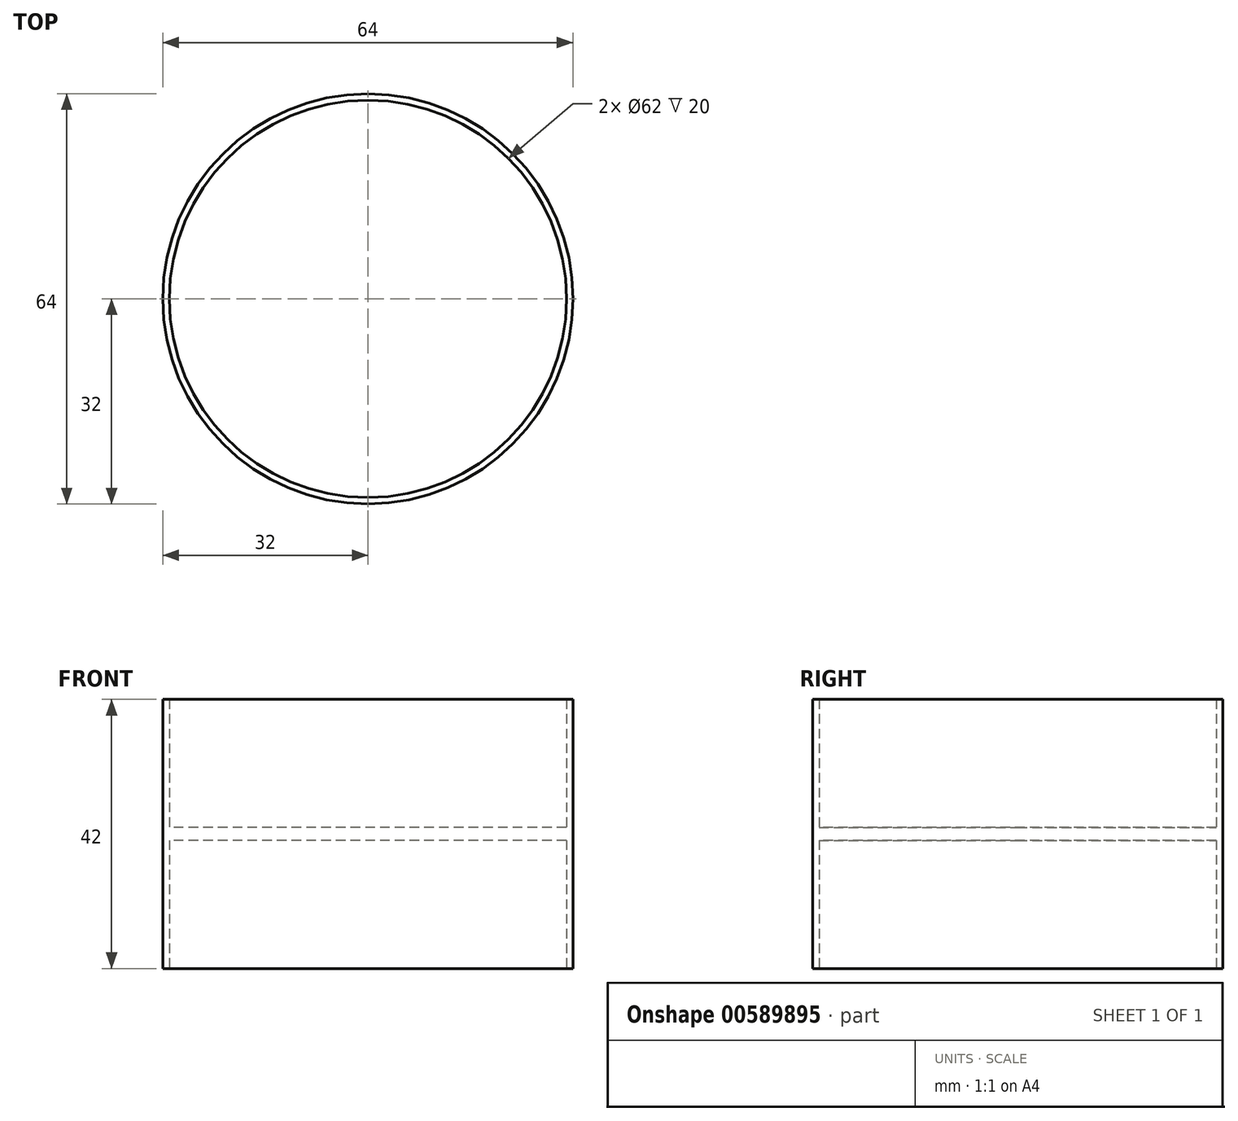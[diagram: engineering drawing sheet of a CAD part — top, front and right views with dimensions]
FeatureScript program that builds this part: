
annotation { "Feature Type Name" : "Feature", "Feature Type Description" : "" }
export const myFeature = defineFeature(function(context is Context, id is Id, definition is map)
    precondition{}
    {
        {
            var Q0;
            Q0=qCreatedBy(makeId("Top.planeOp"),FACE);
            var sketch = newSketch(context, id + "F0", { "sketchPlane" : qUnion([Q0])});
            skCircle(sketch, "E0", {"center": v(0, 0) * mm, "radius": 32 * mm});
            skCircle(sketch, "E1", {"center": v(0, 0) * mm, "radius": 34 * mm});
            skCircle(sketch, "E2", {"center": v(0, 0) * mm, "radius": 31 * mm});
            skLineSegment(sketch, "E3", {"start": v(0, 32) * mm, "end": v(0, -32) * mm});
            skSolve(sketch);
        }
        {
            var Q0;
            {var subQ0=sQuery(id+"F0.wireOp",EDGE,"E3");var subQ1=sQuery(id+"F0.wireOp",EDGE,"E0");var subQ2=makeQuery(id+"F0.imprint","INTERSECT",VERTEX,{"disambiguationData":[OD(0.0)],"derivedFrom":[subQ1,subQ0]});Q0=makeQuery(id+"F0.imprint","IMPRINT",FACE,{"disambiguationData":[TD([[makeQuery(id+"F0.imprint","IMPRINT",EDGE,{"disambiguationData":[TD([[subQ2,-1.0]])],"derivedFrom":subQ1}),1.0]])]});}
            var Q1;
            {var subQ0=sQuery(id+"F0.wireOp",EDGE,"E3");var subQ1=sQuery(id+"F0.wireOp",EDGE,"E0");var subQ2=makeQuery(id+"F0.imprint","INTERSECT",VERTEX,{"disambiguationData":[OD(0.0)],"derivedFrom":[subQ1,subQ0]});Q1=makeQuery(id+"F0.imprint","IMPRINT",FACE,{"disambiguationData":[TD([[makeQuery(id+"F0.imprint","IMPRINT",EDGE,{"disambiguationData":[TD([[subQ2,1.0]])],"derivedFrom":subQ1}),1.0]])]});}
            extrude(context, id + "F1", {"entities" : qUnion([Q0, Q1]), "depth" : 20 * mm, "offsetDistance" : 25 * mm});
        }
        {
            var Q0;
            {var subQ0=sQuery(id+"F0.wireOp",EDGE,"E3");var subQ1=sQuery(id+"F0.wireOp",EDGE,"E0");var subQ2=makeQuery(id+"F0.imprint","INTERSECT",VERTEX,{"disambiguationData":[OD(0.0)],"derivedFrom":[subQ1,subQ0]});Q0=makeQuery(id+"F0.imprint","IMPRINT",FACE,{"disambiguationData":[TD([[makeQuery(id+"F0.imprint","IMPRINT",EDGE,{"disambiguationData":[TD([[subQ2,-1.0]])],"derivedFrom":subQ1}),1.0]])]});}
            var Q1;
            {var subQ0=sQuery(id+"F0.wireOp",EDGE,"E3");var subQ1=sQuery(id+"F0.wireOp",EDGE,"E0");var subQ2=makeQuery(id+"F0.imprint","INTERSECT",VERTEX,{"disambiguationData":[OD(0.0)],"derivedFrom":[subQ1,subQ0]});Q1=makeQuery(id+"F0.imprint","IMPRINT",FACE,{"disambiguationData":[TD([[makeQuery(id+"F0.imprint","IMPRINT",EDGE,{"disambiguationData":[TD([[subQ2,1.0]])],"derivedFrom":subQ1}),1.0]])]});}
            extrude(context, id + "F2", {"entities" : qUnion([Q0, Q1]), "operationType" : NewBodyOperationType.ADD, "oppositeDirection" : true, "depth" : 22 * mm, "offsetDistance" : 25 * mm});
        }
        {
            var Q0;
            {var subQ0=sQuery(id+"F0.wireOp",EDGE,"E3");var subQ1=sQuery(id+"F0.wireOp",EDGE,"E2");var subQ2=makeQuery(id+"F0.imprint","INTERSECT",VERTEX,{"disambiguationData":[OD(0.0)],"derivedFrom":[subQ1,subQ0]});Q0=makeQuery(id+"F0.imprint","IMPRINT",FACE,{"disambiguationData":[TD([[makeQuery(id+"F0.imprint","IMPRINT",EDGE,{"disambiguationData":[TD([[subQ2,-1.0]])],"derivedFrom":subQ1}),1.0]])]});}
            var Q1;
            {var subQ0=sQuery(id+"F0.wireOp",EDGE,"E3");var subQ1=sQuery(id+"F0.wireOp",EDGE,"E2");var subQ2=makeQuery(id+"F0.imprint","INTERSECT",VERTEX,{"disambiguationData":[OD(0.0)],"derivedFrom":[subQ1,subQ0]});Q1=makeQuery(id+"F0.imprint","IMPRINT",FACE,{"disambiguationData":[TD([[makeQuery(id+"F0.imprint","IMPRINT",EDGE,{"disambiguationData":[TD([[subQ2,1.0]])],"derivedFrom":subQ1}),1.0]])]});}
            var Q2;
            {var subQ0=sQuery(id+"F0.wireOp",EDGE,"E3");var subQ1=sQuery(id+"F0.wireOp",EDGE,"E0");var subQ2=makeQuery(id+"F0.imprint","INTERSECT",VERTEX,{"disambiguationData":[OD(0.0)],"derivedFrom":[subQ1,subQ0]});Q2=makeQuery(id+"F0.imprint","IMPRINT",FACE,{"disambiguationData":[TD([[makeQuery(id+"F0.imprint","IMPRINT",EDGE,{"disambiguationData":[TD([[subQ2,1.0]])],"derivedFrom":subQ1}),1.0]])]});}
            var Q3;
            {var subQ0=sQuery(id+"F0.wireOp",EDGE,"E3");var subQ1=sQuery(id+"F0.wireOp",EDGE,"E0");var subQ2=makeQuery(id+"F0.imprint","INTERSECT",VERTEX,{"disambiguationData":[OD(0.0)],"derivedFrom":[subQ1,subQ0]});Q3=makeQuery(id+"F0.imprint","IMPRINT",FACE,{"disambiguationData":[TD([[makeQuery(id+"F0.imprint","IMPRINT",EDGE,{"disambiguationData":[TD([[subQ2,-1.0]])],"derivedFrom":subQ1}),1.0]])]});}
            extrude(context, id + "F3", {"entities" : qUnion([Q0, Q1, Q2, Q3]), "operationType" : NewBodyOperationType.ADD, "oppositeDirection" : true, "depth" : 2 * mm, "offsetDistance" : 25 * mm});
        }
    });
